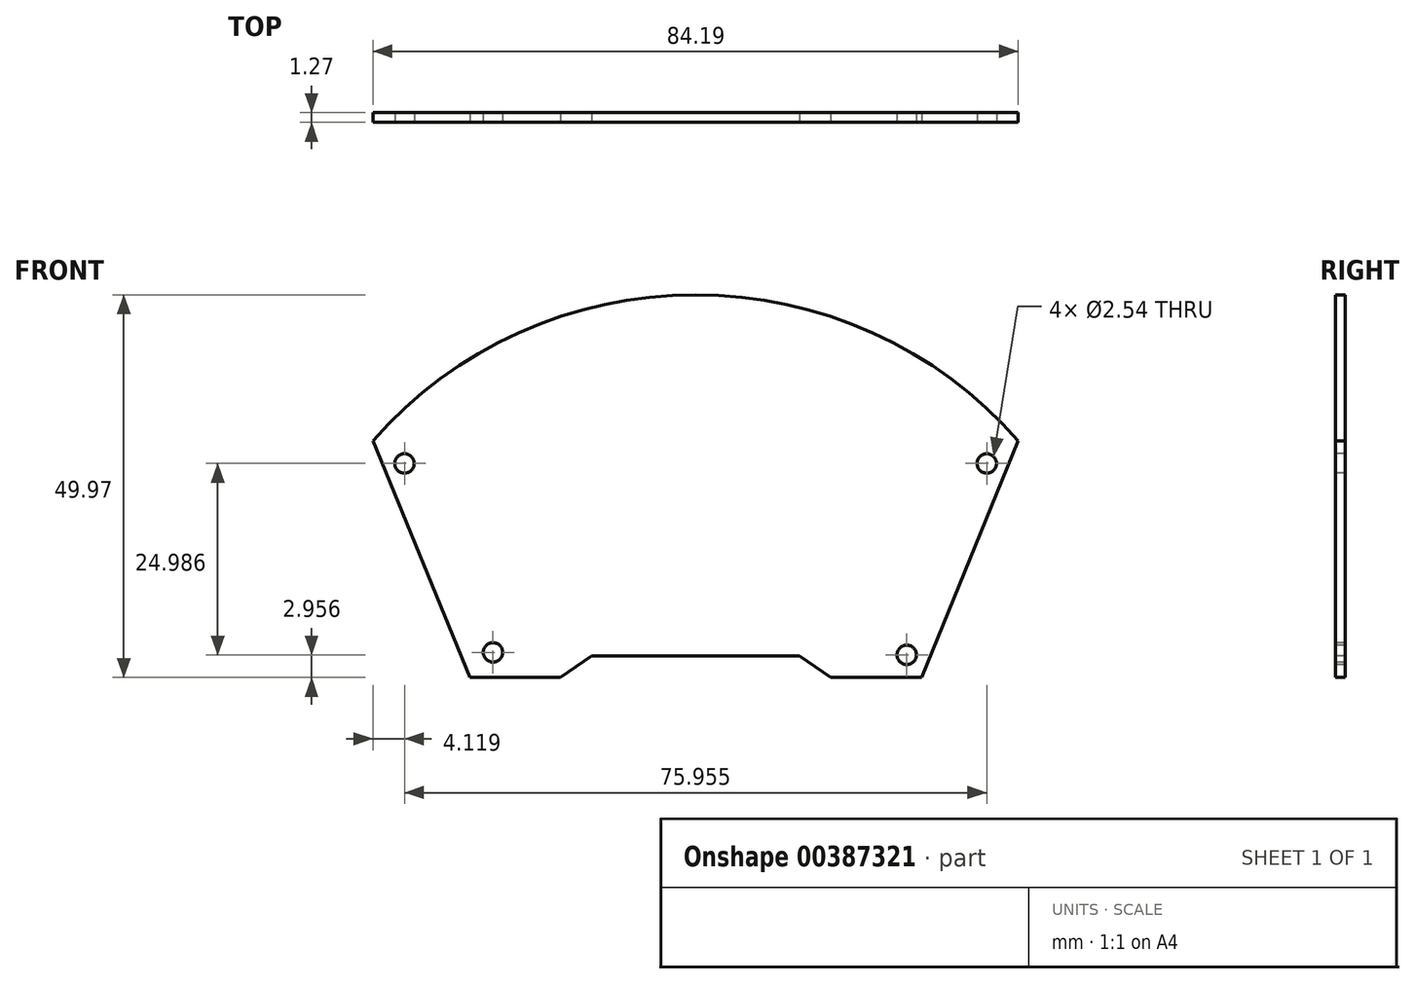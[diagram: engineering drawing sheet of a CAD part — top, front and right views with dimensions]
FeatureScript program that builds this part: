
annotation { "Feature Type Name" : "Feature", "Feature Type Description" : "" }
export const myFeature = defineFeature(function(context is Context, id is Id, definition is map)
    precondition{}
    {
        {
            var Q0;
            Q0=qCreatedBy(makeId("Front.planeOp"),FACE);
            var sketch = newSketch(context, id + "F0", { "sketchPlane" : qUnion([Q0])});
            skPoint(sketch, "E0.orphan", {"position": v(0, 41.93) * mm});
            skLineSegment(sketch, "E1", {"start": v(0, 0) * mm, "end": v(-12.64, -30.92) * mm});
            skLineSegment(sketch, "E2", {"start": v(-12.64, -30.92) * mm, "end": v(-24.46, -30.92) * mm});
            skLineSegment(sketch, "E3", {"start": v(-71.55, -30.92) * mm, "end": v(-84.19, 0) * mm});
            skArc(sketch, "E4", {"start": v(0, 0) * mm, "mid": v(-42.1, 19.05) * mm, "end": v(-84.19, 0) * mm});
            skPoint(sketch, "E5", {"position": v(-68.52, -27.64) * mm});
            skPoint(sketch, "E6", {"position": v(-14.55, -27.96) * mm});
            skPoint(sketch, "E7", {"position": v(-80.07, -2.98) * mm});
            skPoint(sketch, "E8", {"position": v(-4.12, -2.98) * mm});
            skLineSegment(sketch, "E9", {"start": v(-59.72, -30.92) * mm, "end": v(-55.63, -28.11) * mm});
            skLineSegment(sketch, "E10", {"start": v(-55.63, -28.11) * mm, "end": v(-28.56, -28.11) * mm});
            skLineSegment(sketch, "E11", {"start": v(-28.56, -28.11) * mm, "end": v(-24.46, -30.92) * mm});
            skLineSegment(sketch, "E12.trimOffspring", {"start": v(-59.72, -30.92) * mm, "end": v(-71.55, -30.92) * mm});
            skLineSegment(sketch, "E13", {"start": v(-84.19, 0) * mm, "end": v(0, 0) * mm});
            skSolve(sketch);
        }
        {
            var Q0;
            Q0=makeQuery(id+"F0.imprint","IMPRINT",FACE,{"disambiguationData":[TD([[makeQuery(id+"F0.imprint","IMPRINT",EDGE,{"derivedFrom":sQuery(id+"F0.wireOp",EDGE,"E1")}),-1.0]])]});
            var Q1;
            Q1=makeQuery(id+"F0.imprint","IMPRINT",FACE,{"disambiguationData":[TD([[makeQuery(id+"F0.imprint","IMPRINT",EDGE,{"derivedFrom":sQuery(id+"F0.wireOp",EDGE,"E4")}),1.0]])]});
            extrude(context, id + "F1", {"entities" : qUnion([Q0, Q1]), "oppositeDirection" : true, "depth" : 1.27 * mm});
        }
        {
            var Q0;
            Q0=sQuery(id+"F0.wireOp",VERTEX,"E7");
            var Q1;
            Q1=sQuery(id+"F0.wireOp",VERTEX,"E8");
            var Q2;
            Q2=sQuery(id+"F0.wireOp",VERTEX,"E6");
            var Q3;
            Q3=sQuery(id+"F0.wireOp",VERTEX,"E5");
            var Q4;
            Q4=makeQuery(id+"F1.opExtrude","SWEPT_BODY",BODY,{"disambiguationData":[OSD([sQuery(id+"F0.wireOp",EDGE,"E1"),sQuery(id+"F0.wireOp",EDGE,"E2"),sQuery(id+"F0.wireOp",EDGE,"E3"),sQuery(id+"F0.wireOp",EDGE,"E4"),sQuery(id+"F0.wireOp",EDGE,"E9"),sQuery(id+"F0.wireOp",EDGE,"E10"),sQuery(id+"F0.wireOp",EDGE,"E11"),sQuery(id+"F0.wireOp",EDGE,"E12.trimOffspring")])]});
            hole(context, id + "F2", {"style" : HoleStyle.SIMPLE, "endStyle" : HoleEndStyle.THROUGH, "holeDiameter" : 2.54 * mm, "isTappedThrough" : true, "tappedDepth" : 12.7 * mm, "tapClearance" : 3, "startFromSketch" : true, "locations" : qUnion([Q0, Q1, Q2, Q3]), "scope" : qUnion([Q4])});
        }
    });
